# Revit family: 09450170
name_source: partatom
category: Plumbing Fixtures
revit_build: Autodesk Revit 2018 (Build: 20170223_1515(x64)
units: mm (PartAtom-declared; Revit-internal decimal feet)

## family parameters
Always vertical = Yes
Cut with Voids When Loaded = No
OmniClass Number = 23.45.55.11
OmniClass Title = Sanitary Components
Part Type = Normal
Room Calculation Point = No
Round Connector Dimension = Use Diameter
Shared = No
Work Plane-Based = No

## types (1)
- 09450170 Body for urinal flusher
    2D/3D/BIM Files URL = http://static.hansa.com
    3D View = https://static.hansa.com
    Additional Features = protected against back-flow in domestic use (according to DIN EN 1717)
    AssetType = Fixed
    BIMObjectName = 09450170
    BaseunitMainMaterial = Brass
    BodyMaterial = Brass
    Brand = HANSA
    Catalog Drawing URL = http://static.hansa.com
    Category = Public & Semi-public
    CloseOffRating = 0
    Color = Black
    Concealed Parts = Gasket sleeve for dry mortarless construction;Mounting box and cover sleeve
    Connection = Direct connection;External thread;with integrated shut-off valve(s)
    Connection Size = G1/2
    Dimension Drawing URL = http://static.hansa.com
    DurationUnit = Year
    EAN Number = 4015474277373
    ETIM Class Number = EC010546 Mechanical control system for shower
    FDV Document URL = http://www.hansa.com
    Features = Concealed unit
    Finish = Polished
    Flow Drawing URL = http://static.hansa.com
    Flow Rate At 300kPa = 0.4 L/s
    FlowCoefficient = 0
    Group = Urinal flusher
    IfcExportAs = IfcValveType
    IfcExportType = FAUCET
    InletConnectionSize = 20 mm  [stored 0.0656168 ft]
    Installation Depth = 58 - 88 mm
    Installation Type = Concealed wall mounting
    Installation and Maintenance Guide URL = http://static.hansa.com
    Interactive AR View URL = https://static.hansa.com
    Manufacturer = HANSA
    ManufacturerName = HANSA
    ManufacturerURL = http://www.hansa.com
    Market = International;Germany;Austria;Belgium;Netherlands;France;Czech Republic;Slovakia;Italy;Spain
    Material = Brass
    Max. Hot Water Supply = 70 °C
    Mechanical Parts = Litter filter(s)
    Mobile Product Information URL = http://mpi.hansa.com
    Model = 09450170 Body for urinal flusher
    ModelReference = 09450170
    NBSDescription = Water supply fittings for baths
    NBSReference = 45-35-70/315
    Name = 09450170 Body for urinal flusher
    Name_en = 09450170 Body for urinal flusher
    NominalHeight = 247 mm
    NominalWidth = 185 mm  [stored 0.606955 ft]
    Pressure Loss With Flow 02ls = 65000.0 Pa
    Product Code = 09450170
    Product Family = HANSAELECTRA
    Product Image URL = http://static.hansa.com
    Product URL = http://static.hansa.com
    Revision = 4
    Sales Package dimensions (LxWxH) = 435 x 270 x 125
    Shape = Sculptured
    Size = 185x102x247 mm
    Technical DataSheet URL = http://www.hansa.com
    UNSPSC Class Number = 30181702 Faucet unit
    URL Declaration of Conformity = http://static.hansa.com
    URL REACH = http://static.hansa.com
    Uniclass2 = Pr_65_52_61_15
    Uniclass2015Description = Concealed intumescent pipe collars
    Uniclass2015Reference = Pr_65_52_61_15
    Version = 4
    VersionDate = 01/07/2022
    Warranty Information URL = http://warranty.hansa.com
    WarrantyDescription = http://warranty.hansa.com
    WarrantyDurationUnit = Year
    Working Pressure = 50 - 1000 kPa
    WorkingPressure = 50 - 1000 kPa

note: [stored X ft] marks values corroborated as IEEE doubles in the binary element streams (Revit-internal decimal feet)

## geometry (parser evidence)
native form markers: Sweep x11
no freeform markers — native parametric forms only
